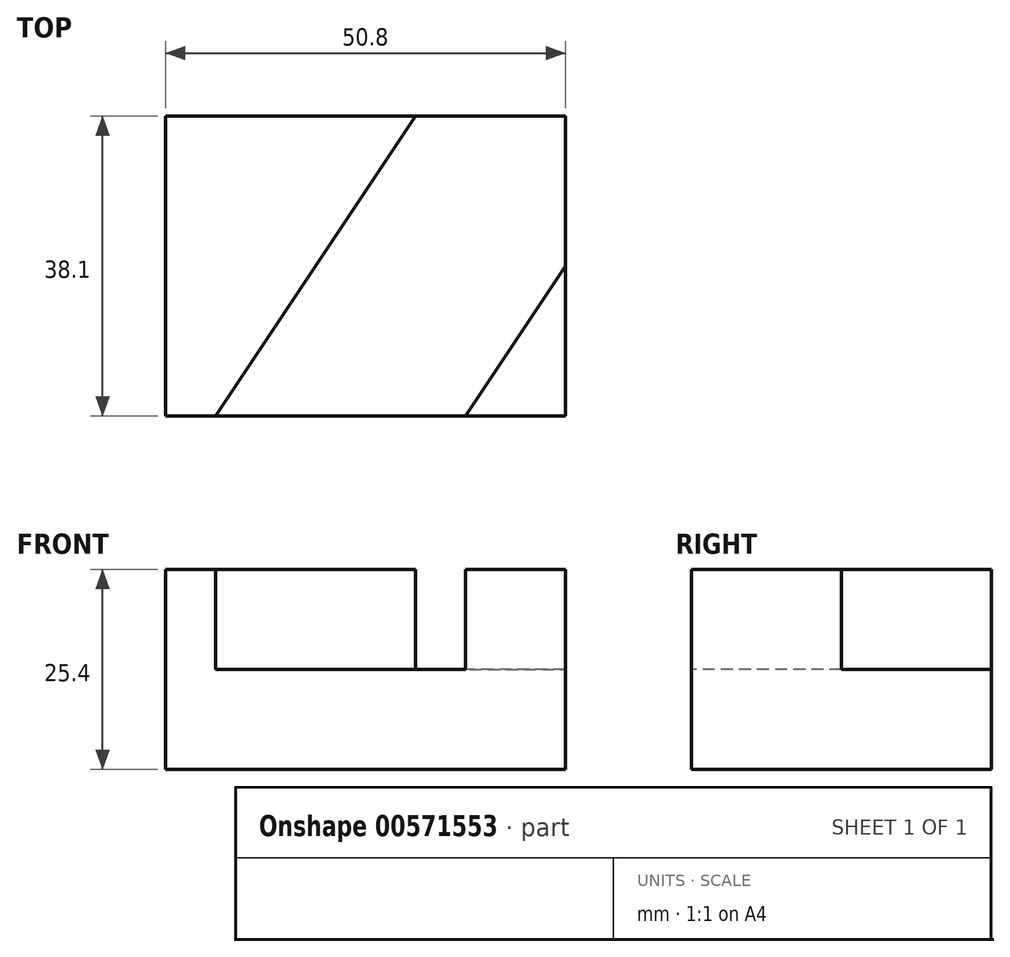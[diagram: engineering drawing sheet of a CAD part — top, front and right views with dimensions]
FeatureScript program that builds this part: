
annotation { "Feature Type Name" : "Feature", "Feature Type Description" : "" }
export const myFeature = defineFeature(function(context is Context, id is Id, definition is map)
    precondition{}
    {
        {
            var Q0;
            Q0=qCreatedBy(makeId("Front.planeOp"),FACE);
            var sketch = newSketch(context, id + "F0", { "sketchPlane" : qUnion([Q0])});
            skLineSegment(sketch, "E0", {"start": v(-64.5, 46.35) * mm, "end": v(-64.5, 20.95) * mm});
            skLineSegment(sketch, "E1", {"start": v(-64.5, 20.95) * mm, "end": v(-13.7, 20.95) * mm});
            skLineSegment(sketch, "E2", {"start": v(-13.7, 20.95) * mm, "end": v(-13.7, 46.35) * mm});
            skLineSegment(sketch, "E3", {"start": v(-13.7, 46.35) * mm, "end": v(-64.5, 46.35) * mm});
            skSolve(sketch);
        }
        {
            var Q0;
            Q0=makeQuery(id+"F0.imprint","IMPRINT",FACE,{"disambiguationData":[TD([[makeQuery(id+"F0.imprint","IMPRINT",EDGE,{"derivedFrom":sQuery(id+"F0.wireOp",EDGE,"E0")}),1.0]])]});
            extrude(context, id + "F1", {"entities" : qUnion([Q0]), "depth" : 38.1 * mm, "offsetDistance" : 25.4 * mm});
        }
        {
            var Q0;
            Q0=makeQuery(id+"F1.opExtrude","CAP_FACE",FACE,{"disambiguationData":[OSD([sQuery(id+"F0.wireOp",EDGE,"E0"),sQuery(id+"F0.wireOp",EDGE,"E1"),sQuery(id+"F0.wireOp",EDGE,"E2"),sQuery(id+"F0.wireOp",EDGE,"E3")])],"isStart":true});
            var sketch = newSketch(context, id + "F2", { "sketchPlane" : qUnion([Q0])});
            skLineSegment(sketch, "E4", {"start": v(32.74, 46.35) * mm, "end": v(32.74, 33.65) * mm});
            skLineSegment(sketch, "E5", {"start": v(32.74, 33.65) * mm, "end": v(13.7, 33.65) * mm});
            skSolve(sketch);
        }
        {
            var Q0;
            {var subQ0=sQuery(id+"F2.wireOp",EDGE,"E4");Q0=makeQuery(id+"F2.imprint","IMPRINT",FACE,{"disambiguationData":[TD([[makeQuery(id+"F2.imprint","IMPRINT",EDGE,{"derivedFrom":subQ0}),-1.0]])]});}
            extrude(context, id + "F3", {"entities" : qUnion([Q0]), "operationType" : NewBodyOperationType.REMOVE, "oppositeDirection" : true, "depth" : 19.05 * mm, "offsetDistance" : 25.4 * mm});
        }
        {
            var Q0;
            Q0=makeQuery(id+"F1.opExtrude","SWEPT_FACE",FACE,{"disambiguationData":[OSD([sQuery(id+"F0.wireOp",EDGE,"E3")])]});
            var sketch = newSketch(context, id + "F4", { "sketchPlane" : qUnion([Q0])});
            skLineSegment(sketch, "E6", {"start": v(-32.74, 0) * mm, "end": v(-58.14, -38.1) * mm});
            skLineSegment(sketch, "E7", {"start": v(-13.7, -19.05) * mm, "end": v(-26.4, -38.1) * mm});
            skSolve(sketch);
        }
        {
            var Q0;
            {var subQ2=sQuery(id+"F4.wireOp",EDGE,"E6");Q0=makeQuery(id+"F4.imprint","IMPRINT",FACE,{"disambiguationData":[TD([[makeQuery(id+"F4.imprint","IMPRINT",EDGE,{"derivedFrom":subQ2}),1.0]])]});}
            extrude(context, id + "F5", {"entities" : qUnion([Q0]), "operationType" : NewBodyOperationType.REMOVE, "oppositeDirection" : true, "depth" : 12.7 * mm, "offsetDistance" : 25.4 * mm});
        }
    });
